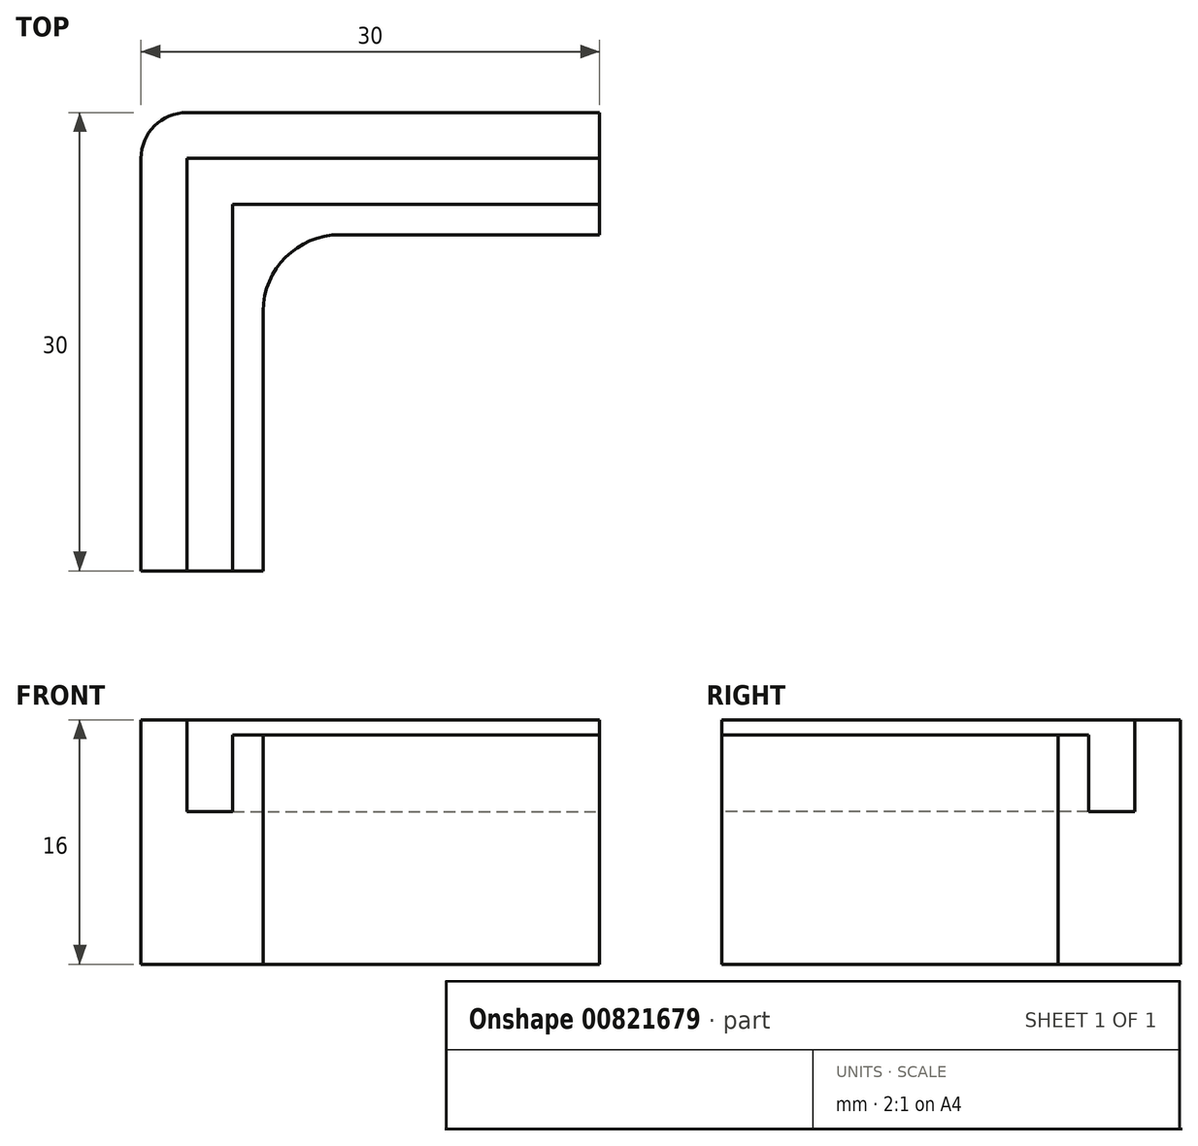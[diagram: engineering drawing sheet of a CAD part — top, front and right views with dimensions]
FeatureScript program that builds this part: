
annotation { "Feature Type Name" : "Feature", "Feature Type Description" : "" }
export const myFeature = defineFeature(function(context is Context, id is Id, definition is map)
    precondition{}
    {
        {
            var Q0;
            Q0=qCreatedBy(makeId("Top.planeOp"),FACE);
            var sketch = newSketch(context, id + "F0", { "sketchPlane" : qUnion([Q0])});
            skLineSegment(sketch, "E0.bottom", {"start": v(-12, 12) * mm, "end": v(12, 12) * mm});
            skLineSegment(sketch, "E0.left", {"start": v(-12, 12) * mm, "end": v(-12, -12) * mm});
            skPoint(sketch, "E0.middle", {"position": v(0, 0) * mm});
            skPoint(sketch, "E0.right.end.orphan", {"position": v(12, -12) * mm});
            skLineSegment(sketch, "E1.0", {"start": v(-15, 15) * mm, "end": v(12, 15) * mm});
            skLineSegment(sketch, "E1.1", {"start": v(-15, 15) * mm, "end": v(-15, -12) * mm});
            skLineSegment(sketch, "E2", {"start": v(12, 15) * mm, "end": v(12, 12) * mm});
            skLineSegment(sketch, "E3", {"start": v(-12, -12) * mm, "end": v(-15, -12) * mm});
            skLineSegment(sketch, "E4.0", {"start": v(-10, 10) * mm, "end": v(12, 10) * mm});
            skLineSegment(sketch, "E4.1", {"start": v(-10, 10) * mm, "end": v(-10, -12) * mm});
            skLineSegment(sketch, "E5.0", {"start": v(-18, 18) * mm, "end": v(12, 18) * mm});
            skLineSegment(sketch, "E5.1", {"start": v(-18, 18) * mm, "end": v(-18, -12) * mm});
            skLineSegment(sketch, "E6", {"start": v(-18, -12) * mm, "end": v(-15, -12) * mm});
            skLineSegment(sketch, "E7", {"start": v(-12, -12) * mm, "end": v(-10, -12) * mm});
            skLineSegment(sketch, "E8", {"start": v(12, 10) * mm, "end": v(12, 12) * mm});
            skLineSegment(sketch, "E9", {"start": v(12, 15) * mm, "end": v(12, 18) * mm});
            skSolve(sketch);
        }
        {
            var Q0;
            Q0 = qSketchRegion(id + "F0", true);
            extrude(context, id + "F1", {"entities" : qUnion([Q0]), "oppositeDirection" : true, "depth" : 10 * mm, "offsetDistance" : 25 * mm});
        }
        {
            var Q0;
            Q0=makeQuery(id+"F0.imprint","IMPRINT",FACE,{"disambiguationData":[TD([[makeQuery(id+"F0.imprint","IMPRINT",EDGE,{"derivedFrom":sQuery(id+"F0.wireOp",EDGE,"E1.0")}),1.0]])]});
            extrude(context, id + "F2", {"entities" : qUnion([Q0]), "operationType" : NewBodyOperationType.ADD, "depth" : 6 * mm, "offsetDistance" : 25 * mm});
        }
        {
            var Q0;
            Q0=makeQuery(id+"F0.imprint","IMPRINT",FACE,{"disambiguationData":[TD([[makeQuery(id+"F0.imprint","IMPRINT",EDGE,{"derivedFrom":sQuery(id+"F0.wireOp",EDGE,"E0.bottom")}),-1.0]])]});
            extrude(context, id + "F3", {"entities" : qUnion([Q0]), "operationType" : NewBodyOperationType.ADD, "depth" : 5 * mm, "offsetDistance" : 25 * mm});
        }
        {
            var Q0;
            {var subQ0=sQuery(id+"F0.wireOp",EDGE,"E4.1");var subQ1=sQuery(id+"F0.wireOp",EDGE,"E4.0");Q0=makeQuery(id+"F3.boolean.opBoolean","MERGE",EDGE,{"derivedFrom":[makeQuery(id+"F1.opExtrude","SWEPT_EDGE",EDGE,{"disambiguationData":[OSD([subQ1,subQ0])]}),makeQuery(id+"F3.opExtrude","SWEPT_EDGE",EDGE,{"disambiguationData":[OSD([subQ1,subQ0])]})]});}
            fillet(context, id + "F4", {"entities" : qUnion([Q0]), "radius" : 5 * mm, "tangentPropagation" : true, "allowEdgeOverflow" : false});
        }
        {
            var Q0;
            {var subQ0=sQuery(id+"F0.wireOp",EDGE,"E5.1");var subQ1=sQuery(id+"F0.wireOp",EDGE,"E5.0");Q0=makeQuery(id+"F2.boolean.opBoolean","MERGE",EDGE,{"derivedFrom":[makeQuery(id+"F1.opExtrude","SWEPT_EDGE",EDGE,{"disambiguationData":[OSD([subQ1,subQ0])]}),makeQuery(id+"F2.opExtrude","SWEPT_EDGE",EDGE,{"disambiguationData":[OSD([subQ1,subQ0])]})]});}
            fillet(context, id + "F5", {"entities" : qUnion([Q0]), "radius" : 3 * mm, "tangentPropagation" : true, "allowEdgeOverflow" : false});
        }
    });
